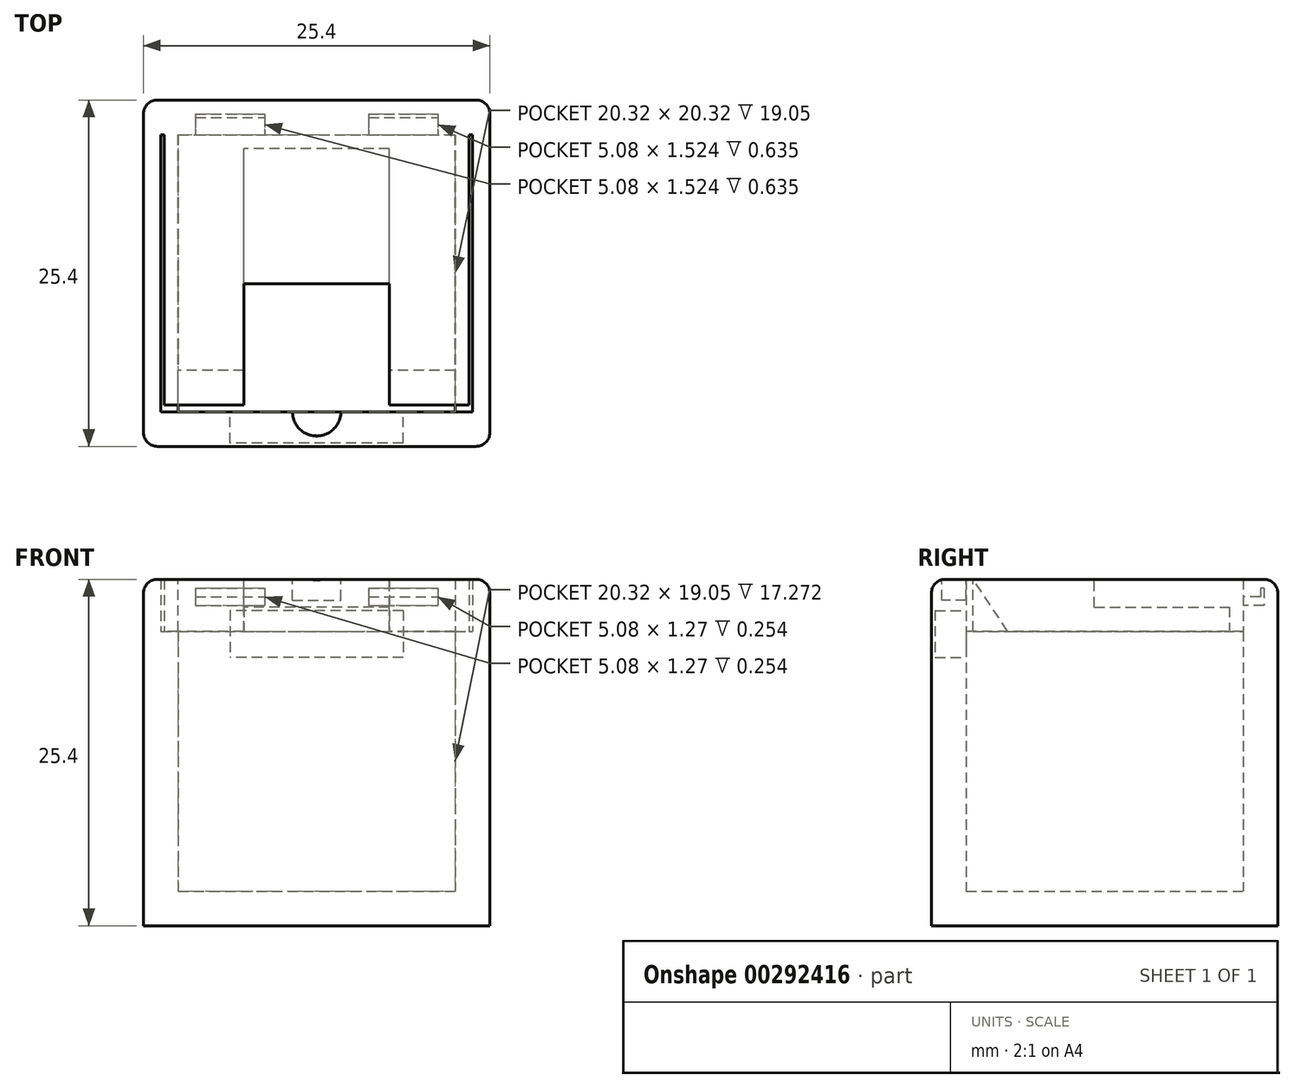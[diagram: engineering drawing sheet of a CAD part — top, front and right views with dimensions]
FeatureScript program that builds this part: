
annotation { "Feature Type Name" : "Feature", "Feature Type Description" : "" }
export const myFeature = defineFeature(function(context is Context, id is Id, definition is map)
    precondition{}
    {
        {
            var Q0;
            Q0=qCreatedBy(makeId("Top.planeOp"),FACE);
            var sketch = newSketch(context, id + "F0", { "sketchPlane" : qUnion([Q0])});
            skLineSegment(sketch, "E0.bottom", {"start": v(-12.7, 12.7) * mm, "end": v(12.7, 12.7) * mm});
            skLineSegment(sketch, "E0.top", {"start": v(-12.7, -12.7) * mm, "end": v(12.7, -12.7) * mm});
            skLineSegment(sketch, "E0.left", {"start": v(-12.7, 12.7) * mm, "end": v(-12.7, -12.7) * mm});
            skLineSegment(sketch, "E0.right", {"start": v(12.7, 12.7) * mm, "end": v(12.7, -12.7) * mm});
            skPoint(sketch, "E1", {"position": v(12.7, 0) * mm});
            skPoint(sketch, "E2", {"position": v(0, 12.7) * mm});
            skPoint(sketch, "E3", {"position": v(0, 0) * mm});
            skLineSegment(sketch, "E4.0", {"start": v(11.43, 10.16) * mm, "end": v(11.43, -10.16) * mm});
            skLineSegment(sketch, "E4.1", {"start": v(-11.43, 10.16) * mm, "end": v(11.43, 10.16) * mm});
            skLineSegment(sketch, "E4.2", {"start": v(-11.43, 10.16) * mm, "end": v(-11.43, -10.16) * mm});
            skLineSegment(sketch, "E4.3", {"start": v(-11.43, -10.16) * mm, "end": v(11.43, -10.16) * mm});
            skLineSegment(sketch, "E5", {"start": v(0, -10.16) * mm, "end": v(0, -12.7) * mm, "construction": true});
            skLineSegment(sketch, "E6", {"start": v(0, 12.7) * mm, "end": v(0, 10.16) * mm, "construction": true});
            skLineSegment(sketch, "E7", {"start": v(-10.16, 10.16) * mm, "end": v(-10.16, -10.16) * mm});
            skLineSegment(sketch, "E8", {"start": v(10.16, 10.16) * mm, "end": v(10.16, -10.16) * mm});
            skLineSegment(sketch, "E9", {"start": v(-10.16, 0) * mm, "end": v(-11.43, 0) * mm, "construction": true});
            skLineSegment(sketch, "E10", {"start": v(10.16, 0) * mm, "end": v(11.43, 0) * mm, "construction": true});
            skLineSegment(sketch, "E11", {"start": v(11.43, 0) * mm, "end": v(12.7, 0) * mm, "construction": true});
            skSolve(sketch);
        }
        {
            var Q0;
            Q0 = qSketchRegion(id + "F0", true);
            extrude(context, id + "F1", {"entities" : qUnion([Q0]), "depth" : 25.4 * mm});
        }
        {
            var Q0;
            Q0 = qSketchRegion(id + "F0", true);
            var Q1;
            Q1=makeQuery(id+"F0.imprint","IMPRINT",FACE,{"disambiguationData":[TD([[makeQuery(id+"F0.imprint","IMPRINT",EDGE,{"derivedFrom":sQuery(id+"F0.wireOp",EDGE,"E4.0")}),-1.0]])]});
            var Q2;
            {var subQ0=sQuery(id+"F0.wireOp",EDGE,"E7");Q2=makeQuery(id+"F0.imprint","IMPRINT",FACE,{"disambiguationData":[TD([[makeQuery(id+"F0.imprint","IMPRINT",EDGE,{"derivedFrom":subQ0}),1.0]])]});}
            var Q3;
            {var subQ0=sQuery(id+"F0.wireOp",EDGE,"E4.2");Q3=makeQuery(id+"F0.imprint","IMPRINT",FACE,{"disambiguationData":[TD([[makeQuery(id+"F0.imprint","IMPRINT",EDGE,{"derivedFrom":subQ0}),1.0]])]});}
            extrude(context, id + "F2", {"entities" : qUnion([Q0, Q1, Q2, Q3]), "operationType" : NewBodyOperationType.ADD, "depth" : 2.54 * mm});
        }
        {
            var Q0;
            {var subQ0=sQuery(id+"F0.wireOp",EDGE,"E4.2");Q0=makeQuery(id+"F0.imprint","IMPRINT",FACE,{"disambiguationData":[TD([[makeQuery(id+"F0.imprint","IMPRINT",EDGE,{"derivedFrom":subQ0}),1.0]])]});}
            var Q1;
            {var subQ0=sQuery(id+"F0.wireOp",EDGE,"E4.0");Q1=makeQuery(id+"F0.imprint","IMPRINT",FACE,{"disambiguationData":[TD([[makeQuery(id+"F0.imprint","IMPRINT",EDGE,{"derivedFrom":subQ0}),-1.0]])]});}
            extrude(context, id + "F3", {"entities" : qUnion([Q0, Q1]), "operationType" : NewBodyOperationType.ADD, "depth" : 21.59 * mm});
        }
        {
            var Q0;
            Q0=makeQuery(id+"F1.opExtrude","CAP_FACE",FACE,{"disambiguationData":[OSD([sQuery(id+"F0.wireOp",EDGE,"E0.bottom"),sQuery(id+"F0.wireOp",EDGE,"E0.top"),sQuery(id+"F0.wireOp",EDGE,"E0.left"),sQuery(id+"F0.wireOp",EDGE,"E0.right"),sQuery(id+"F0.wireOp",EDGE,"E4.0"),sQuery(id+"F0.wireOp",EDGE,"E4.1"),sQuery(id+"F0.wireOp",EDGE,"E4.2"),sQuery(id+"F0.wireOp",EDGE,"E4.3")])],"isStart":false});
            var sketch = newSketch(context, id + "F4", { "sketchPlane" : qUnion([Q0])});
            skLineSegment(sketch, "E12.bottom", {"start": v(-12.83, 12.83) * mm, "end": v(12.83, 12.83) * mm});
            skLineSegment(sketch, "E12.top", {"start": v(-12.83, -12.83) * mm, "end": v(12.83, -12.83) * mm});
            skLineSegment(sketch, "E12.left", {"start": v(-12.83, 12.83) * mm, "end": v(-12.83, -12.83) * mm});
            skLineSegment(sketch, "E12.right", {"start": v(12.83, 12.83) * mm, "end": v(12.83, -12.83) * mm});
            skLineSegment(sketch, "E13.0", {"start": v(-14.1, 14.1) * mm, "end": v(14.1, 14.1) * mm});
            skLineSegment(sketch, "E13.1", {"start": v(-14.1, 14.1) * mm, "end": v(-14.1, -14.1) * mm});
            skLineSegment(sketch, "E13.2", {"start": v(-14.1, -14.1) * mm, "end": v(14.1, -14.1) * mm});
            skLineSegment(sketch, "E13.3", {"start": v(14.1, 14.1) * mm, "end": v(14.1, -14.1) * mm});
            skPoint(sketch, "E14", {"position": v(0, 12.83) * mm});
            skPoint(sketch, "E15", {"position": v(-12.83, 0) * mm});
            skSolve(sketch);
        }
        {
            var Q0;
            Q0=makeQuery(id+"F4.imprint","IMPRINT",FACE,{"disambiguationData":[TD([[makeQuery(id+"F4.imprint","IMPRINT",EDGE,{"derivedFrom":sQuery(id+"F4.wireOp",EDGE,"E12.bottom")}),-1.0]])]});
            var Q1;
            Q1=makeQuery(id+"F4.imprint","IMPRINT",FACE,{"disambiguationData":[TD([[makeQuery(id+"F4.imprint","IMPRINT",EDGE,{"derivedFrom":sQuery(id+"F4.wireOp",EDGE,"E12.bottom")}),1.0]])]});
            var Q2;
            Q2=makeQuery(id+"F4.imprint","IMPRINT",FACE,{"disambiguationData":[TD([[makeQuery(id+"F4.imprint","IMPRINT",EDGE,{"derivedFrom":makeQuery(id+"F1.opExtrude","CAP_EDGE",EDGE,{"disambiguationData":[OSD([sQuery(id+"F0.wireOp",EDGE,"E0.bottom")])],"isStart":false})}),-1.0]])]});
            var Q3;
            Q3=makeQuery(id+"F4.imprint","IMPRINT",FACE,{"disambiguationData":[TD([[makeQuery(id+"F4.imprint","IMPRINT",EDGE,{"derivedFrom":makeQuery(id+"F1.opExtrude","CAP_EDGE",EDGE,{"disambiguationData":[OSD([sQuery(id+"F0.wireOp",EDGE,"E4.0")])],"isStart":false})}),-1.0]])]});
            extrude(context, id + "F5", {"entities" : qUnion([Q0, Q1, Q2, Q3]), "depth" : 1.27 * mm});
        }
        {
            var Q0;
            Q0 = qSketchRegion(id + "F4", true);
            extrude(context, id + "F6", {"entities" : qUnion([Q0]), "operationType" : NewBodyOperationType.ADD, "oppositeDirection" : true, "depth" : 2.54 * mm});
        }
        {
            var Q0;
            Q0=makeQuery(id+"F5.opExtrude","SWEPT_BODY",BODY,{"disambiguationData":[OSD([sQuery(id+"F4.wireOp",EDGE,"E13.0"),sQuery(id+"F4.wireOp",EDGE,"E13.1"),sQuery(id+"F4.wireOp",EDGE,"E13.2"),sQuery(id+"F4.wireOp",EDGE,"E13.3")])]});
            deleteBodies(context, id + "F7", {"entities" : qUnion([Q0])});
        }
        {
            var Q0;
            Q0=makeQuery(id+"F1.opExtrude","SWEPT_FACE",FACE,{"disambiguationData":[OSD([sQuery(id+"F0.wireOp",EDGE,"E4.1")])]});
            var sketch = newSketch(context, id + "F8", { "sketchPlane" : qUnion([Q0])});
            skLineSegment(sketch, "E16.bottom", {"start": v(-8.9, 24.77) * mm, "end": v(-3.81, 24.77) * mm});
            skLineSegment(sketch, "E16.top", {"start": v(-8.9, 23.5) * mm, "end": v(-3.81, 23.5) * mm});
            skLineSegment(sketch, "E16.left", {"start": v(-8.9, 24.77) * mm, "end": v(-8.9, 23.5) * mm});
            skLineSegment(sketch, "E16.right", {"start": v(-3.81, 24.77) * mm, "end": v(-3.81, 23.5) * mm});
            skLineSegment(sketch, "E17.bottom", {"start": v(3.81, 24.77) * mm, "end": v(8.9, 24.77) * mm});
            skLineSegment(sketch, "E17.top", {"start": v(3.81, 23.5) * mm, "end": v(8.9, 23.5) * mm});
            skLineSegment(sketch, "E17.left", {"start": v(3.81, 24.77) * mm, "end": v(3.81, 23.5) * mm});
            skLineSegment(sketch, "E17.right", {"start": v(8.9, 24.77) * mm, "end": v(8.9, 23.5) * mm});
            skLineSegment(sketch, "E18", {"start": v(3.81, 24.77) * mm, "end": v(0, 24.77) * mm, "construction": true});
            skLineSegment(sketch, "E19", {"start": v(-3.81, 24.77) * mm, "end": v(0, 24.77) * mm, "construction": true});
            skLineSegment(sketch, "E20", {"start": v(0, 25.4) * mm, "end": v(0, 23.37) * mm, "construction": true});
            skLineSegment(sketch, "E21", {"start": v(5.33, 23.37) * mm, "end": v(-5.33, 23.37) * mm});
            skPoint(sketch, "E22", {"position": v(0, 23.37) * mm});
            skLineSegment(sketch, "E23", {"start": v(-5.33, 23.37) * mm, "end": v(-5.33, 21.59) * mm});
            skLineSegment(sketch, "E24", {"start": v(-5.33, 21.59) * mm, "end": v(5.33, 21.6) * mm});
            skLineSegment(sketch, "E25", {"start": v(5.33, 21.59) * mm, "end": v(5.33, 23.37) * mm});
            skLineSegment(sketch, "E26", {"start": v(-5.33, 21.59) * mm, "end": v(-11.43, 21.59) * mm});
            skLineSegment(sketch, "E27", {"start": v(5.33, 21.59) * mm, "end": v(11.43, 21.59) * mm});
            skPoint(sketch, "E28", {"position": v(-8.9, 24.13) * mm});
            skPoint(sketch, "E29", {"position": v(-3.81, 24.13) * mm});
            skPoint(sketch, "E30", {"position": v(3.81, 24.13) * mm});
            skPoint(sketch, "E31", {"position": v(8.9, 24.13) * mm});
            skLineSegment(sketch, "E32", {"start": v(-8.9, 24.13) * mm, "end": v(-3.81, 24.13) * mm});
            skLineSegment(sketch, "E33", {"start": v(3.81, 24.13) * mm, "end": v(8.9, 24.13) * mm});
            skLineSegment(sketch, "E34", {"start": v(-11.43, 21.59) * mm, "end": v(-11.43, 25.4) * mm, "construction": true});
            skLineSegment(sketch, "E35", {"start": v(-11.43, 25.4) * mm, "end": v(11.43, 25.4) * mm});
            skLineSegment(sketch, "E36", {"start": v(11.43, 25.4) * mm, "end": v(11.43, 21.6) * mm, "construction": true});
            skLineSegment(sketch, "E37", {"start": v(-11.18, 25.4) * mm, "end": v(-11.18, 21.59) * mm});
            skLineSegment(sketch, "E38", {"start": v(-11.18, 23.5) * mm, "end": v(-11.43, 23.5) * mm, "construction": true});
            skLineSegment(sketch, "E39", {"start": v(11.18, 25.4) * mm, "end": v(11.18, 21.6) * mm});
            skLineSegment(sketch, "E40", {"start": v(11.18, 23.5) * mm, "end": v(11.43, 23.5) * mm, "construction": true});
            skSolve(sketch);
        }
        {
            var Q0;
            {var subQ0=sQuery(id+"F8.wireOp",EDGE,"E16.top");Q0=makeQuery(id+"F8.imprint","IMPRINT",FACE,{"disambiguationData":[TD([[makeQuery(id+"F8.imprint","IMPRINT",EDGE,{"derivedFrom":subQ0}),1.0]])]});}
            var Q1;
            {var subQ0=sQuery(id+"F8.wireOp",EDGE,"E16.bottom");Q1=makeQuery(id+"F8.imprint","IMPRINT",FACE,{"disambiguationData":[TD([[makeQuery(id+"F8.imprint","IMPRINT",EDGE,{"derivedFrom":subQ0}),-1.0]])]});}
            var Q2;
            {var subQ0=sQuery(id+"F8.wireOp",EDGE,"E17.top");Q2=makeQuery(id+"F8.imprint","IMPRINT",FACE,{"disambiguationData":[TD([[makeQuery(id+"F8.imprint","IMPRINT",EDGE,{"derivedFrom":subQ0}),1.0]])]});}
            var Q3;
            {var subQ0=sQuery(id+"F8.wireOp",EDGE,"E17.bottom");Q3=makeQuery(id+"F8.imprint","IMPRINT",FACE,{"disambiguationData":[TD([[makeQuery(id+"F8.imprint","IMPRINT",EDGE,{"derivedFrom":subQ0}),-1.0]])]});}
            extrude(context, id + "F9", {"entities" : qUnion([Q0, Q1, Q2, Q3]), "operationType" : NewBodyOperationType.REMOVE, "oppositeDirection" : true, "depth" : 1.52 * mm});
        }
        {
            var Q0;
            Q0=makeQuery(id+"F1.opExtrude","SWEPT_FACE",FACE,{"disambiguationData":[OSD([sQuery(id+"F0.wireOp",EDGE,"E4.3")])]});
            var sketch = newSketch(context, id + "F10", { "sketchPlane" : qUnion([Q0])});
            skLineSegment(sketch, "E41.bottom", {"start": v(-6.35, 23.11) * mm, "end": v(6.35, 23.11) * mm});
            skLineSegment(sketch, "E41.top", {"start": v(-6.35, 19.68) * mm, "end": v(6.35, 19.68) * mm});
            skLineSegment(sketch, "E41.left", {"start": v(-6.35, 23.11) * mm, "end": v(-6.35, 19.68) * mm});
            skLineSegment(sketch, "E41.right", {"start": v(6.35, 23.11) * mm, "end": v(6.35, 19.68) * mm});
            skPoint(sketch, "E42", {"position": v(0, 23.11) * mm});
            skSolve(sketch);
        }
        {
            var Q0;
            Q0=makeQuery(id+"F10.imprint","IMPRINT",FACE,{"disambiguationData":[TD([[makeQuery(id+"F10.imprint","IMPRINT",EDGE,{"derivedFrom":sQuery(id+"F10.wireOp",EDGE,"E41.bottom")}),-1.0]])]});
            extrude(context, id + "F11", {"entities" : qUnion([Q0]), "operationType" : NewBodyOperationType.REMOVE, "oppositeDirection" : true, "depth" : 2.3 * mm});
        }
        {
            var Q0;
            Q0=makeQuery(id+"F1.opExtrude","CAP_FACE",FACE,{"disambiguationData":[OSD([sQuery(id+"F0.wireOp",EDGE,"E0.bottom"),sQuery(id+"F0.wireOp",EDGE,"E0.top"),sQuery(id+"F0.wireOp",EDGE,"E0.left"),sQuery(id+"F0.wireOp",EDGE,"E0.right"),sQuery(id+"F0.wireOp",EDGE,"E4.0"),sQuery(id+"F0.wireOp",EDGE,"E4.1"),sQuery(id+"F0.wireOp",EDGE,"E4.2"),sQuery(id+"F0.wireOp",EDGE,"E4.3")])],"isStart":false});
            var sketch = newSketch(context, id + "F12", { "sketchPlane" : qUnion([Q0])});
            skArc(sketch, "E43", {"start": v(-1.78, -10.16) * mm, "mid": v(0, -11.94) * mm, "end": v(1.78, -10.16) * mm});
            skSolve(sketch);
        }
        {
            var Q0;
            {var subQ0=sQuery(id+"F12.wireOp",EDGE,"E43");var subQ1=makeQuery(id+"F1.opExtrude","CAP_EDGE",EDGE,{"disambiguationData":[OSD([sQuery(id+"F0.wireOp",EDGE,"E4.3")])],"isStart":false});var subQ2=makeQuery(id+"F12.imprint","INTERSECT",VERTEX,{"disambiguationData":[OD(0.0)],"derivedFrom":[subQ1,subQ0]});Q0=makeQuery(id+"F12.imprint","IMPRINT",FACE,{"disambiguationData":[TD([[makeQuery(id+"F12.imprint","IMPRINT",EDGE,{"disambiguationData":[TD([[subQ2,-1.0]])],"derivedFrom":subQ0}),1.0]])]});}
            extrude(context, id + "F13", {"entities" : qUnion([Q0]), "operationType" : NewBodyOperationType.REMOVE, "oppositeDirection" : true, "depth" : 1.52 * mm});
        }
        {
            var Q0;
            {var subQ0=sQuery(id+"F8.wireOp",EDGE,"E17.bottom");Q0=makeQuery(id+"F8.imprint","IMPRINT",FACE,{"disambiguationData":[TD([[makeQuery(id+"F8.imprint","IMPRINT",EDGE,{"derivedFrom":subQ0}),-1.0]])]});}
            var Q1;
            {var subQ0=sQuery(id+"F8.wireOp",EDGE,"E16.bottom");Q1=makeQuery(id+"F8.imprint","IMPRINT",FACE,{"disambiguationData":[TD([[makeQuery(id+"F8.imprint","IMPRINT",EDGE,{"derivedFrom":subQ0}),-1.0]])]});}
            extrude(context, id + "F14", {"entities" : qUnion([Q0, Q1]), "oppositeDirection" : true, "depth" : 1.27 * mm});
        }
        {
            var Q0;
            {var subQ9=sQuery(id+"F8.wireOp",EDGE,"E16.bottom");Q0=makeQuery(id+"F8.imprint","IMPRINT",FACE,{"disambiguationData":[TD([[makeQuery(id+"F8.imprint","IMPRINT",EDGE,{"derivedFrom":subQ9}),1.0]])]});}
            var Q1;
            {var subQ0=sQuery(id+"F8.wireOp",EDGE,"E17.bottom");Q1=makeQuery(id+"F8.imprint","IMPRINT",FACE,{"disambiguationData":[TD([[makeQuery(id+"F8.imprint","IMPRINT",EDGE,{"derivedFrom":subQ0}),-1.0]])]});}
            var Q2;
            {var subQ0=sQuery(id+"F8.wireOp",EDGE,"E17.top");Q2=makeQuery(id+"F8.imprint","IMPRINT",FACE,{"disambiguationData":[TD([[makeQuery(id+"F8.imprint","IMPRINT",EDGE,{"derivedFrom":subQ0}),1.0]])]});}
            var Q3;
            {var subQ0=sQuery(id+"F8.wireOp",EDGE,"E16.bottom");Q3=makeQuery(id+"F8.imprint","IMPRINT",FACE,{"disambiguationData":[TD([[makeQuery(id+"F8.imprint","IMPRINT",EDGE,{"derivedFrom":subQ0}),-1.0]])]});}
            var Q4;
            {var subQ0=sQuery(id+"F8.wireOp",EDGE,"E16.top");Q4=makeQuery(id+"F8.imprint","IMPRINT",FACE,{"disambiguationData":[TD([[makeQuery(id+"F8.imprint","IMPRINT",EDGE,{"derivedFrom":subQ0}),1.0]])]});}
            extrude(context, id + "F15", {"entities" : qUnion([Q0, Q1, Q2, Q3, Q4]), "operationType" : NewBodyOperationType.ADD, "depth" : 19.8 * mm});
        }
        {
            var Q0;
            Q0=makeQuery(id+"F8.imprint","IMPRINT",FACE,{"disambiguationData":[TD([[makeQuery(id+"F8.imprint","IMPRINT",EDGE,{"derivedFrom":sQuery(id+"F8.wireOp",EDGE,"E21")}),1.0]])]});
            extrude(context, id + "F16", {"entities" : qUnion([Q0]), "operationType" : NewBodyOperationType.ADD, "depth" : 1.02 * mm});
        }
        {
            var Q0;
            Q0=makeQuery(id+"F15.opExtrude","SWEPT_FACE",FACE,{"disambiguationData":[OSD([sQuery(id+"F8.wireOp",EDGE,"E35")])]});
            var sketch = newSketch(context, id + "F17", { "sketchPlane" : qUnion([Q0])});
            skLineSegment(sketch, "E44.bottom", {"start": v(-5.33, -9.65) * mm, "end": v(5.33, -9.65) * mm});
            skLineSegment(sketch, "E44.top", {"start": v(-5.33, -0.76) * mm, "end": v(5.33, -0.76) * mm});
            skLineSegment(sketch, "E44.left", {"start": v(-5.33, -9.65) * mm, "end": v(-5.33, -0.76) * mm});
            skLineSegment(sketch, "E44.right", {"start": v(5.33, -9.65) * mm, "end": v(5.33, -0.76) * mm});
            skPoint(sketch, "E45", {"position": v(0, -0.76) * mm});
            skSolve(sketch);
        }
        {
            var Q0;
            Q0=makeQuery(id+"F17.imprint","IMPRINT",FACE,{"disambiguationData":[TD([[makeQuery(id+"F17.imprint","IMPRINT",EDGE,{"derivedFrom":sQuery(id+"F17.wireOp",EDGE,"E44.bottom")}),1.0]])]});
            extrude(context, id + "F18", {"entities" : qUnion([Q0]), "operationType" : NewBodyOperationType.REMOVE, "oppositeDirection" : true, "depth" : 5.08 * mm});
        }
        {
            var Q0;
            Q0=makeQuery(id+"F15.opExtrude","CAP_EDGE",EDGE,{"disambiguationData":[OSD([sQuery(id+"F8.wireOp",EDGE,"E26")])],"isStart":false});
            var Q1;
            Q1=makeQuery(id+"F15.opExtrude","CAP_EDGE",EDGE,{"disambiguationData":[OSD([sQuery(id+"F8.wireOp",EDGE,"E27")])],"isStart":false});
            chamfer(context, id + "F19", {"entities" : qUnion([Q0, Q1]), "chamferType" : ChamferType.TWO_OFFSETS, "width1" : 2.54 * mm, "oppositeDirection" : false, "width2" : 3.8 * mm, "tangentPropagation" : true});
        }
        {
            var Q0;
            Q0=makeQuery(id+"F1.opExtrude","SWEPT_EDGE",EDGE,{"disambiguationData":[OSD([sQuery(id+"F0.wireOp",EDGE,"E0.top"),sQuery(id+"F0.wireOp",EDGE,"E0.right")])]});
            var Q1;
            Q1=makeQuery(id+"F1.opExtrude","CAP_EDGE",EDGE,{"disambiguationData":[OSD([sQuery(id+"F0.wireOp",EDGE,"E0.right")])],"isStart":false});
            var Q2;
            Q2=makeQuery(id+"F1.opExtrude","CAP_EDGE",EDGE,{"disambiguationData":[OSD([sQuery(id+"F0.wireOp",EDGE,"E0.top")])],"isStart":false});
            var Q3;
            Q3=makeQuery(id+"F1.opExtrude","CAP_EDGE",EDGE,{"disambiguationData":[OSD([sQuery(id+"F0.wireOp",EDGE,"E0.left")])],"isStart":false});
            var Q4;
            Q4=makeQuery(id+"F1.opExtrude","SWEPT_EDGE",EDGE,{"disambiguationData":[OSD([sQuery(id+"F0.wireOp",EDGE,"E0.top"),sQuery(id+"F0.wireOp",EDGE,"E0.left")])]});
            var Q5;
            Q5=makeQuery(id+"F1.opExtrude","SWEPT_EDGE",EDGE,{"disambiguationData":[OSD([sQuery(id+"F0.wireOp",EDGE,"E0.bottom"),sQuery(id+"F0.wireOp",EDGE,"E0.right")])]});
            var Q6;
            Q6=makeQuery(id+"F1.opExtrude","CAP_EDGE",EDGE,{"disambiguationData":[OSD([sQuery(id+"F0.wireOp",EDGE,"E0.bottom")])],"isStart":false});
            var Q7;
            Q7=makeQuery(id+"F1.opExtrude","SWEPT_EDGE",EDGE,{"disambiguationData":[OSD([sQuery(id+"F0.wireOp",EDGE,"E0.bottom"),sQuery(id+"F0.wireOp",EDGE,"E0.left")])]});
            fillet(context, id + "F20", {"entities" : qUnion([Q0, Q1, Q2, Q3, Q4, Q5, Q6, Q7]), "radius" : 1.02 * mm, "tangentPropagation" : true, "allowEdgeOverflow" : false});
        }
    });
